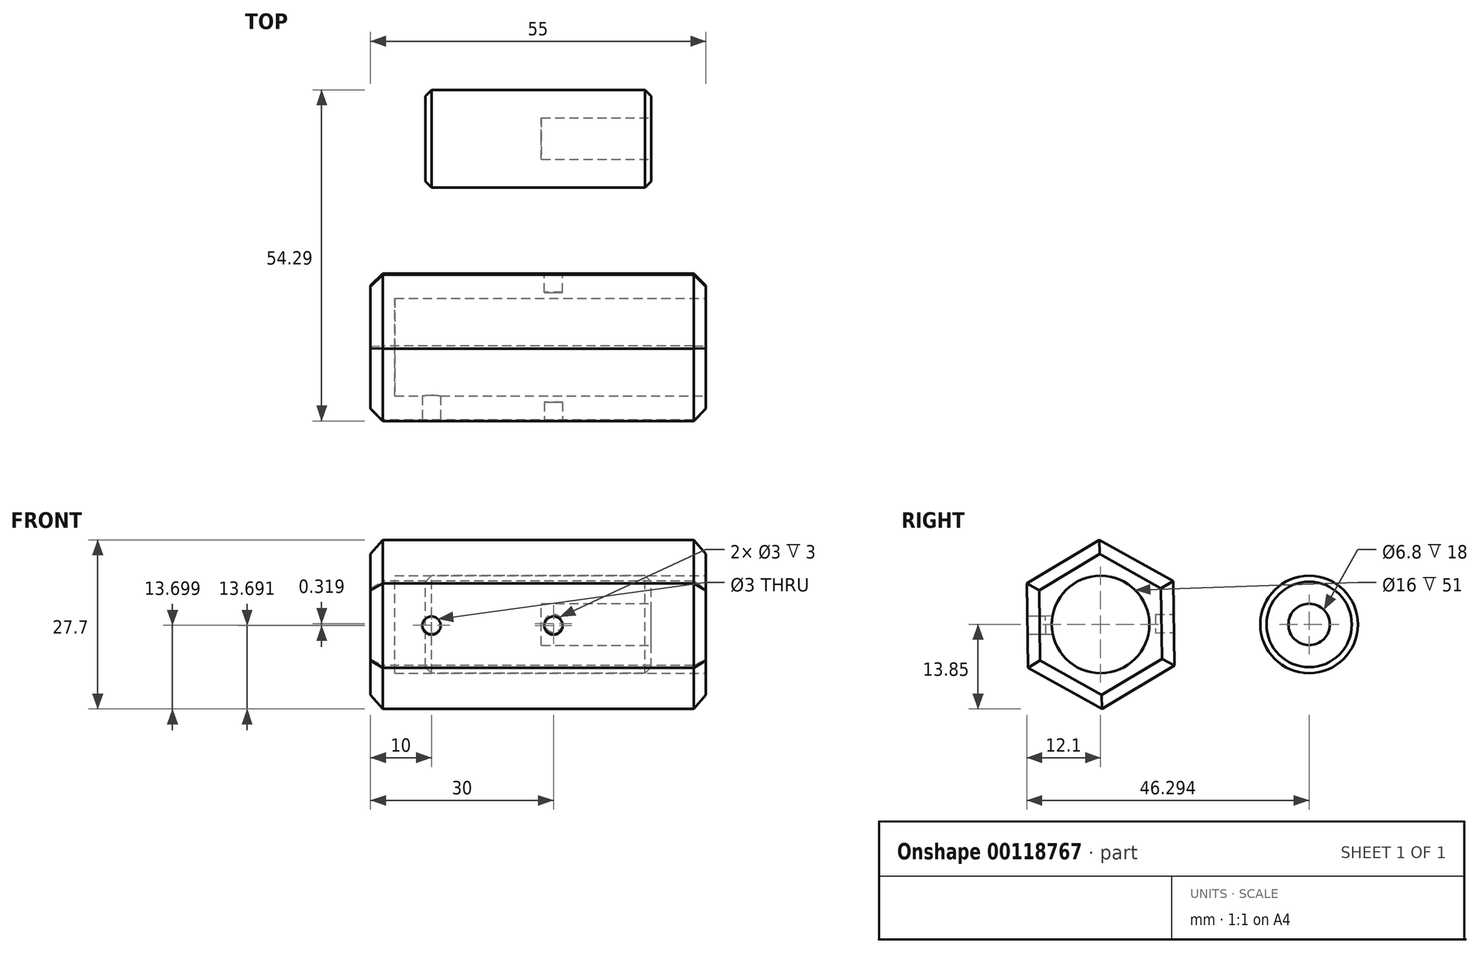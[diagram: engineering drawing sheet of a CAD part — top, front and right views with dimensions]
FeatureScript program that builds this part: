
annotation { "Feature Type Name" : "Feature", "Feature Type Description" : "" }
export const myFeature = defineFeature(function(context is Context, id is Id, definition is map)
    precondition{}
    {
        {
            var Q0;
            Q0=qCreatedBy(makeId("Right.planeOp"),FACE);
            var sketch = newSketch(context, id + "F0", { "sketchPlane" : qUnion([Q0])});
            skCircle(sketch, "E0.cCircle", {"center": v(0, 0) * mm, "radius": 12 * mm, "construction": true});
            skLineSegment(sketch, "E0.0", {"start": v(0.21, -13.85) * mm, "end": v(-11.9, -7.1) * mm});
            skLineSegment(sketch, "E0.1", {"start": v(-11.9, -7.1) * mm, "end": v(-12.1, 6.75) * mm});
            skLineSegment(sketch, "E0.2", {"start": v(-12.1, 6.75) * mm, "end": v(-0.21, 13.85) * mm});
            skLineSegment(sketch, "E0.3", {"start": v(-0.21, 13.85) * mm, "end": v(11.9, 7.1) * mm});
            skLineSegment(sketch, "E0.4", {"start": v(11.9, 7.1) * mm, "end": v(12.1, -6.75) * mm});
            skLineSegment(sketch, "E0.5", {"start": v(12.1, -6.75) * mm, "end": v(0.21, -13.85) * mm});
            skPoint(sketch, "E0.0.midPoint", {"position": v(-5.84, -10.48) * mm});
            skSolve(sketch);
        }
        {
            var Q0;
            Q0 = qSketchRegion(id + "F0", true);
            extrude(context, id + "F1", {"entities" : qUnion([Q0]), "endBound" : BoundingType.SYMMETRIC, "depth" : 55 * mm});
        }
        {
            var Q0;
            Q0=makeQuery(id+"F1.opExtrude","CAP_FACE",FACE,{"disambiguationData":[OSD([sQuery(id+"F0.wireOp",EDGE,"E0.0"),sQuery(id+"F0.wireOp",EDGE,"E0.1"),sQuery(id+"F0.wireOp",EDGE,"E0.2"),sQuery(id+"F0.wireOp",EDGE,"E0.3"),sQuery(id+"F0.wireOp",EDGE,"E0.4"),sQuery(id+"F0.wireOp",EDGE,"E0.5")])],"isStart":false});
            var sketch = newSketch(context, id + "F2", { "sketchPlane" : qUnion([Q0])});
            skCircle(sketch, "E1", {"center": v(0, 0) * mm, "radius": 8 * mm});
            skSolve(sketch);
        }
        {
            var Q0;
            Q0 = qSketchRegion(id + "F2", true);
            extrude(context, id + "F3", {"entities" : qUnion([Q0]), "operationType" : NewBodyOperationType.REMOVE, "oppositeDirection" : true, "depth" : 51 * mm});
        }
        {
            var Q0;
            Q0=makeQuery(id+"F1.opExtrude","SWEPT_FACE",FACE,{"disambiguationData":[OSD([sQuery(id+"F0.wireOp",EDGE,"E0.1")])]});
            var sketch = newSketch(context, id + "F4", { "sketchPlane" : qUnion([Q0])});
            skLineSegment(sketch, "E2", {"start": v(-27.5, 0) * mm, "end": v(2.5, 0) * mm});
            skLineSegment(sketch, "E3", {"start": v(2.5, 0) * mm, "end": v(-17.5, 0) * mm});
            skCircle(sketch, "E4", {"center": v(2.5, 0) * mm, "radius": 1.5 * mm});
            skSolve(sketch);
        }
        {
            var Q0;
            Q0 = qSketchRegion(id + "F4", true);
            extrude(context, id + "F5", {"entities" : qUnion([Q0]), "operationType" : NewBodyOperationType.REMOVE, "oppositeDirection" : true, "depth" : 3 * mm});
        }
        {
            var Q0;
            Q0=makeQuery(id+"F1.opExtrude","SWEPT_FACE",FACE,{"disambiguationData":[OSD([sQuery(id+"F0.wireOp",EDGE,"E0.1")])]});
            var sketch = newSketch(context, id + "F6", { "sketchPlane" : qUnion([Q0])});
            skLineSegment(sketch, "E5", {"start": v(2.5, 0) * mm, "end": v(-17.5, 0) * mm});
            skCircle(sketch, "E6", {"center": v(-17.5, 0) * mm, "radius": 1.5 * mm});
            skSolve(sketch);
        }
        {
            var Q0;
            Q0 = qSketchRegion(id + "F6", true);
            extrude(context, id + "F7", {"entities" : qUnion([Q0]), "operationType" : NewBodyOperationType.REMOVE, "oppositeDirection" : true, "depth" : 5 * mm});
        }
        {
            var Q0;
            Q0=makeQuery(id+"F1.opExtrude","SWEPT_FACE",FACE,{"disambiguationData":[OSD([sQuery(id+"F0.wireOp",EDGE,"E0.4")])]});
            var sketch = newSketch(context, id + "F8", { "sketchPlane" : qUnion([Q0])});
            skLineSegment(sketch, "E7", {"start": v(27.5, 0) * mm, "end": v(-2.5, 0) * mm});
            skCircle(sketch, "E8", {"center": v(-2.5, 0) * mm, "radius": 1.5 * mm});
            skSolve(sketch);
        }
        {
            var Q0;
            Q0 = qSketchRegion(id + "F8", true);
            extrude(context, id + "F9", {"entities" : qUnion([Q0]), "operationType" : NewBodyOperationType.REMOVE, "oppositeDirection" : true, "depth" : 3 * mm});
        }
        {
            var Q0;
            Q0=makeQuery(id+"F1.opExtrude","CAP_EDGE",EDGE,{"disambiguationData":[OSD([sQuery(id+"F0.wireOp",EDGE,"E0.2")])],"isStart":false});
            var Q1;
            Q1=makeQuery(id+"F1.opExtrude","CAP_EDGE",EDGE,{"disambiguationData":[OSD([sQuery(id+"F0.wireOp",EDGE,"E0.1")])],"isStart":false});
            var Q2;
            Q2=makeQuery(id+"F1.opExtrude","CAP_EDGE",EDGE,{"disambiguationData":[OSD([sQuery(id+"F0.wireOp",EDGE,"E0.0")])],"isStart":false});
            var Q3;
            Q3=makeQuery(id+"F1.opExtrude","CAP_EDGE",EDGE,{"disambiguationData":[OSD([sQuery(id+"F0.wireOp",EDGE,"E0.5")])],"isStart":false});
            var Q4;
            Q4=makeQuery(id+"F1.opExtrude","CAP_EDGE",EDGE,{"disambiguationData":[OSD([sQuery(id+"F0.wireOp",EDGE,"E0.4")])],"isStart":false});
            var Q5;
            Q5=makeQuery(id+"F1.opExtrude","CAP_EDGE",EDGE,{"disambiguationData":[OSD([sQuery(id+"F0.wireOp",EDGE,"E0.3")])],"isStart":false});
            var Q6;
            Q6=makeQuery(id+"F1.opExtrude","CAP_EDGE",EDGE,{"disambiguationData":[OSD([sQuery(id+"F0.wireOp",EDGE,"E0.3")])],"isStart":true});
            var Q7;
            Q7=makeQuery(id+"F1.opExtrude","CAP_EDGE",EDGE,{"disambiguationData":[OSD([sQuery(id+"F0.wireOp",EDGE,"E0.2")])],"isStart":true});
            var Q8;
            Q8=makeQuery(id+"F1.opExtrude","CAP_EDGE",EDGE,{"disambiguationData":[OSD([sQuery(id+"F0.wireOp",EDGE,"E0.1")])],"isStart":true});
            var Q9;
            Q9=makeQuery(id+"F1.opExtrude","CAP_EDGE",EDGE,{"disambiguationData":[OSD([sQuery(id+"F0.wireOp",EDGE,"E0.0")])],"isStart":true});
            var Q10;
            Q10=makeQuery(id+"F1.opExtrude","CAP_EDGE",EDGE,{"disambiguationData":[OSD([sQuery(id+"F0.wireOp",EDGE,"E0.5")])],"isStart":true});
            var Q11;
            Q11=makeQuery(id+"F1.opExtrude","CAP_EDGE",EDGE,{"disambiguationData":[OSD([sQuery(id+"F0.wireOp",EDGE,"E0.4")])],"isStart":true});
            chamfer(context, id + "F10", {"entities" : qUnion([Q0, Q1, Q2, Q3, Q4, Q5, Q6, Q7, Q8, Q9, Q10, Q11]), "width" : 2 * mm, "tangentPropagation" : true});
        }
        {
            var Q0;
            Q0=qCreatedBy(makeId("Right.planeOp"),FACE);
            var sketch = newSketch(context, id + "F11", { "sketchPlane" : qUnion([Q0])});
            skCircle(sketch, "E9", {"center": v(34.2, 0) * mm, "radius": 8 * mm});
            skSolve(sketch);
        }
        {
            var Q0;
            Q0 = qSketchRegion(id + "F11", true);
            extrude(context, id + "F12", {"entities" : qUnion([Q0]), "endBound" : BoundingType.SYMMETRIC, "depth" : 37 * mm});
        }
        {
            var Q0;
            Q0=makeQuery(id+"F12.opExtrude","CAP_FACE",FACE,{"disambiguationData":[OSD([sQuery(id+"F11.wireOp",EDGE,"E9")])],"isStart":false});
            var sketch = newSketch(context, id + "F13", { "sketchPlane" : qUnion([Q0])});
            skCircle(sketch, "E10", {"center": v(34.2, 0) * mm, "radius": 3.4 * mm});
            skSolve(sketch);
        }
        {
            var Q0;
            Q0 = qSketchRegion(id + "F13", true);
            extrude(context, id + "F14", {"entities" : qUnion([Q0]), "operationType" : NewBodyOperationType.REMOVE, "oppositeDirection" : true, "depth" : 18 * mm});
        }
        {
            var Q0;
            Q0=makeQuery(id+"F12.opExtrude","CAP_EDGE",EDGE,{"disambiguationData":[OSD([sQuery(id+"F11.wireOp",EDGE,"E9")])],"isStart":false});
            var Q1;
            Q1=makeQuery(id+"F12.opExtrude","CAP_EDGE",EDGE,{"disambiguationData":[OSD([sQuery(id+"F11.wireOp",EDGE,"E9")])],"isStart":true});
            chamfer(context, id + "F15", {"entities" : qUnion([Q0, Q1]), "width" : 1 * mm, "tangentPropagation" : true});
        }
    });
